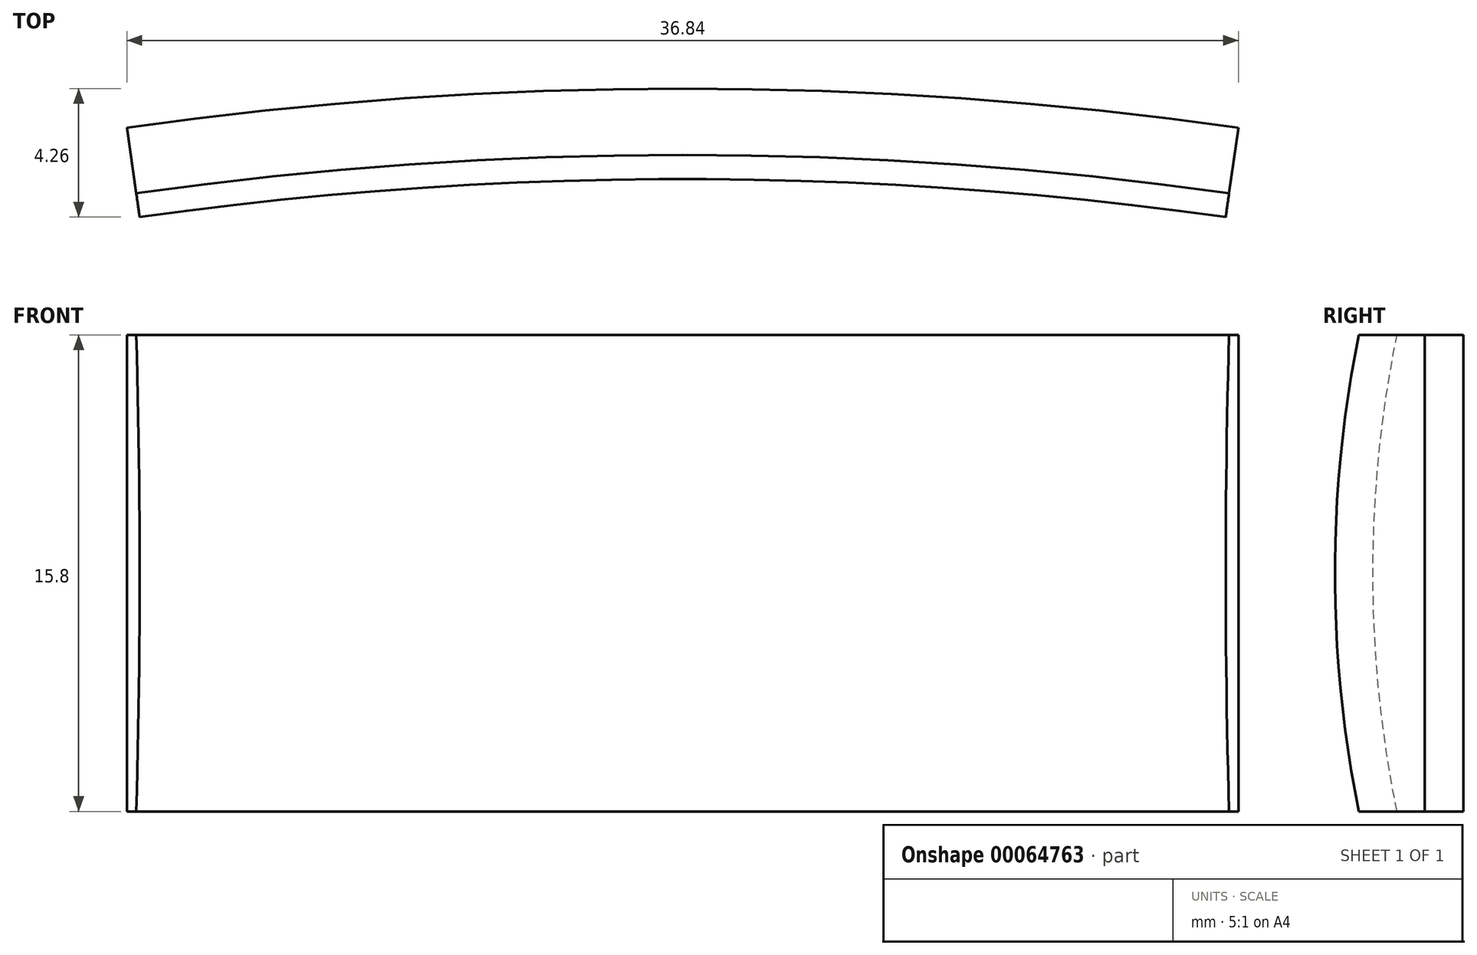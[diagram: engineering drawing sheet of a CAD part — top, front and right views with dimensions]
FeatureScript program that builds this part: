
annotation { "Feature Type Name" : "Feature", "Feature Type Description" : "" }
export const myFeature = defineFeature(function(context is Context, id is Id, definition is map)
    precondition{}
    {
        {
            var Q0;
            Q0=qCreatedBy(makeId("Top.planeOp"),FACE);
            var sketch = newSketch(context, id + "F0", { "sketchPlane" : qUnion([Q0])});
            skArc(sketch, "E0", {"start": v(36, 0) * mm, "mid": v(18, 1.26) * mm, "end": v(0, 0) * mm});
            skSolve(sketch);
        }
        {
            var Q0;
            Q0=sQuery(id+"F0.wireOp",EDGE,"E0");
            var Q1;
            Q1=sQuery(id+"F0.wireOp",VERTEX,"E0.end");
            cPlane(context, id + "F1", {"entities" : qUnion([Q0, Q1]), "cplaneType" : CPlaneType.CURVE_POINT, "offset" : 150 * mm, "width" : 150 * mm, "height" : 150 * mm});
        }
        {
            var Q0;
            Q0=qCreatedBy(id+"F1.planeOp",FACE);
            var sketch = newSketch(context, id + "F2", { "sketchPlane" : qUnion([Q0])});
            skLineSegment(sketch, "E1", {"start": v(-3, -7.9) * mm, "end": v(-3, 7.9) * mm});
            skLineSegment(sketch, "E2", {"start": v(-3, 7.9) * mm, "end": v(-0.8, 7.9) * mm});
            skLineSegment(sketch, "E3", {"start": v(-3, -7.9) * mm, "end": v(-0.8, -7.9) * mm});
            skArc(sketch, "E4", {"start": v(-0.8, -7.9) * mm, "mid": v(0, 0) * mm, "end": v(-0.8, 7.9) * mm});
            skPoint(sketch, "E5", {"position": v(0, 0) * mm});
            skSolve(sketch);
        }
        {
            var Q0;
            Q0=makeQuery(id+"F2.imprint","IMPRINT",FACE,{"disambiguationData":[TD([[makeQuery(id+"F2.imprint","IMPRINT",EDGE,{"derivedFrom":sQuery(id+"F2.wireOp",EDGE,"E1")}),-1.0]])]});
            var Q1;
            Q1=sQuery(id+"F0.wireOp",EDGE,"E0");
            sweep(context, id + "F3", {"profiles" : qUnion([Q0]), "path" : qUnion([Q1])});
        }
    });
